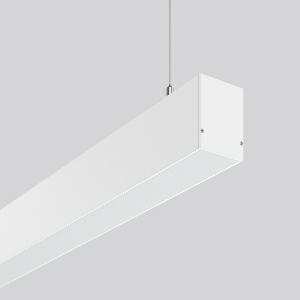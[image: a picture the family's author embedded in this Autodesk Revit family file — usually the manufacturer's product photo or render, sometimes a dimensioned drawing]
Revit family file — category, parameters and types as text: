
# Revit family: less_is_more_50_312319_002_1_76_da18
name_source: partatom
category: Lighting Fixtures
units: mm (PartAtom-declared; Revit-internal decimal feet)

## family parameters
Cut with Voids When Loaded = No
Host = Face
Light Source = No
Part Type = Normal
Room Calculation Point = No
Round Connector Dimension = Use Diameter
Shared = No

## types (1)
- LESS IS MORE 50 (1 x LED Modul 840, 6450 lm, 4000)
    Apparent Load = 52 VA
    CIE Flux Codes = 49 80 96 63 100
    Color Rendering = 80
    Color Temperature = 4000
    Default Elevation = 1800 mm
    Description = Series: LESS IS MORE 50
Linear pendant luminaire for aesthetically sophisticated lighting. Housing: extruded aluminium profile, powder-coated. End cap aluminium powder-coated. Canopy made of aluminium, powder-coated. Diffuser made of non-yellowing plastic (PMMA), opal. Direct 65%, indirect 35% light emission. Suitable for pendant. 2-point steel cable suspension freely positionable and infinitely height-adjustable. Special lengths available on request. LED unit with integrated converter interchangeable and removable. Suitable for through-wiring. With sensors or as a safety luminaire on request. 
Colour: traffic white, matt (RAL 9016)
Length: 1407 mm
Width: 57 mm
Height: 75 mm
Suspension length: 2000 mm
Lamp: LED
Socket: without socket
Colour temperature: 4000K
Colour rendering index (CRI): 80
Light source: LED
Socket lamp2: Without base
Colour temperature: 4000K
System power: 52 W
Rated luminous flux: 6450 lm
Luminous efficiency: 124 lm/W
Control gear: Converter, dimmable, DALI
Control gear: Converter, dimmable, DALI
Protection class: I
Type of protection: IP 20
    Height = 75 mm
    Lamp = 1 x LED Modul 840
    Lamp Light Flux = 6450 lm
    Lamp count = 1
    Length = 1407 mm
    Lifetime = 50000 h
    Luminous efficacy = 124 lm/W
    Manufacturer = RZB
    ModVariant = No
    Model = 312319.002.1.76
    Mounting Place = Ceiling
    Mounting Type = Pendant
    Number of Poles = 1
    OnlyDefault = Yes
    Power Factor = 1
    Product Name = LESS IS MORE 50
    Product group = Pendant LED linear luminaires
    ProductGroupID = 907
    Protection Class = Protection class I
    Protection Degree = IP 20
    RLX_Detail_Level = 1
    RLX_Emergency_Light_Flux = 0 lm
    RLX_Emergency_Type = 0
    RLX_Emergency_Type_DB = No
    RlxData = <blob elided: 31641 chars, md5=ee8d8463>
    Socket = socket
    Standby Power = 0 W
    System Light Flux = 6450 lm
    System Power = 52 W
    Type Comments = Product without accessories
    Type Image = 312318.002.jpg
    URL = http://relux.com
    VarID = ---
    Voltage = 230 V
    Voltage Range = 220-240 V
    Weight = 0.00 kg
    Width = 57 mm

## geometry (parser evidence)
native form markers: Blend x4, Sweep x13
no freeform markers — native parametric forms only
